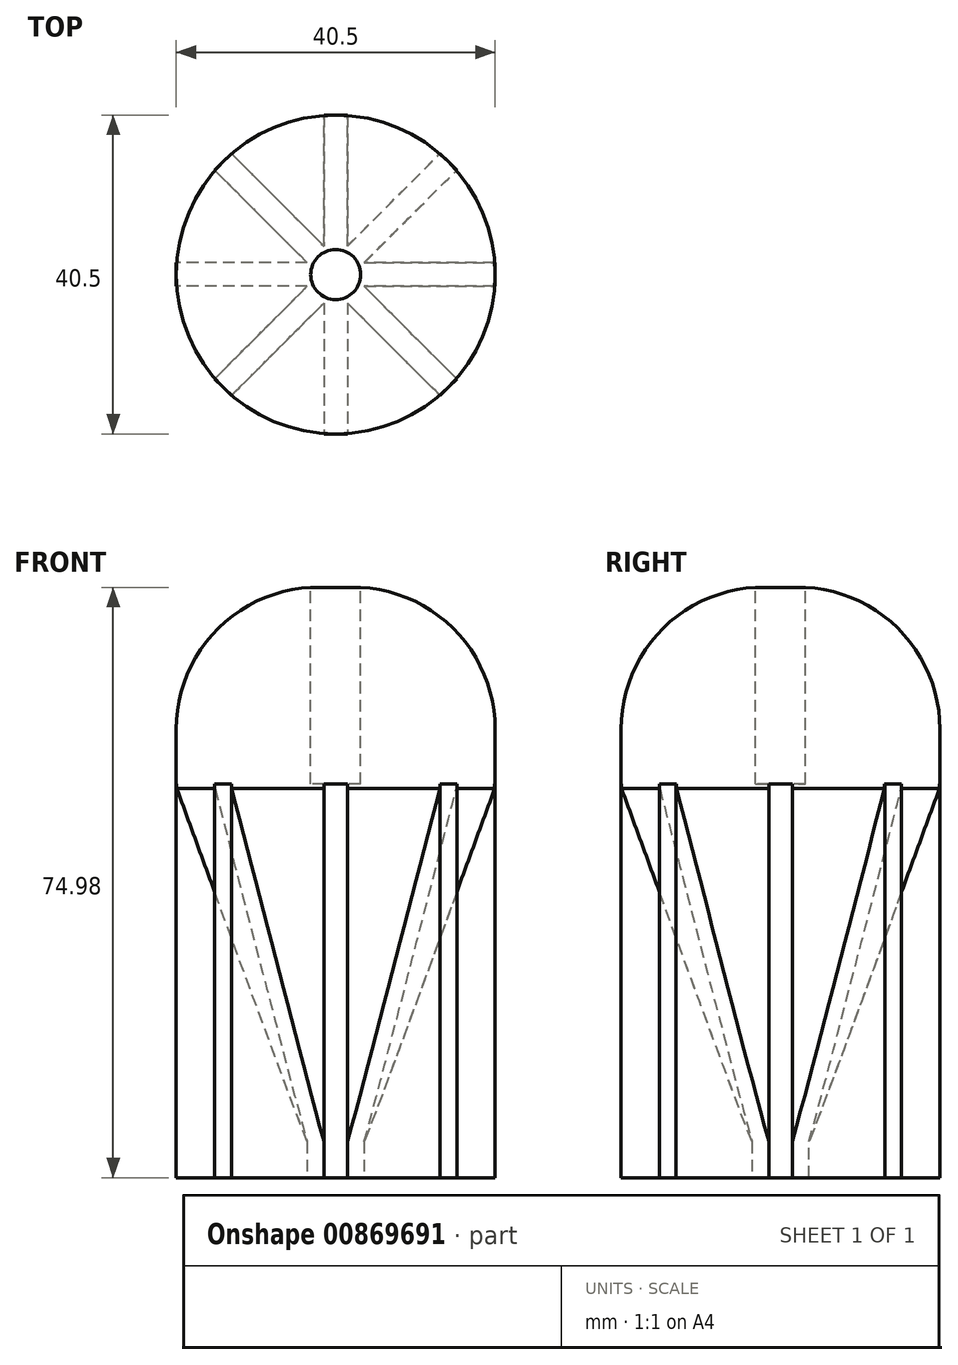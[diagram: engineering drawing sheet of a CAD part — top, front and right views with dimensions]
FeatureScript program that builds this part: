
annotation { "Feature Type Name" : "Feature", "Feature Type Description" : "" }
export const myFeature = defineFeature(function(context is Context, id is Id, definition is map)
    precondition{}
    {
        {
            var Q0;
            Q0=qCreatedBy(makeId("Top.planeOp"),FACE);
            var sketch = newSketch(context, id + "F0", { "sketchPlane" : qUnion([Q0])});
            skCircle(sketch, "E0", {"center": v(0, 0) * mm, "radius": 20.25 * mm});
            skSolve(sketch);
        }
        {
            var Q0;
            Q0 = qSketchRegion(id + "F0", true);
            extrude(context, id + "F1", {"entities" : qUnion([Q0]), "depth" : 75 * mm, "offsetDistance" : 25 * mm});
        }
        {
            var Q0;
            Q0=makeQuery(id+"F1.opExtrude","CAP_EDGE",EDGE,{"disambiguationData":[OSD([sQuery(id+"F0.wireOp",EDGE,"E0")])],"isStart":true});
            chamfer(context, id + "F2", {"entities" : qUnion([Q0]), "chamferType" : ChamferType.OFFSET_ANGLE, "width" : 18 * mm, "oppositeDirection" : true, "angle" : 70 * degree, "tangentPropagation" : true});
        }
        {
            var Q0;
            Q0=makeQuery(id+"F1.opExtrude","CAP_FACE",FACE,{"disambiguationData":[OSD([sQuery(id+"F0.wireOp",EDGE,"E0")])],"isStart":false});
            fillet(context, id + "F3", {"entities" : qUnion([Q0]), "radius" : 18 * mm, "tangentPropagation" : true, "allowEdgeOverflow" : false});
        }
        {
            var Q0;
            Q0=makeQuery(id+"F1.opExtrude","CAP_FACE",FACE,{"disambiguationData":[OSD([sQuery(id+"F0.wireOp",EDGE,"E0")])],"isStart":true});
            var sketch = newSketch(context, id + "F4", { "sketchPlane" : qUnion([Q0])});
            skCircle(sketch, "E1", {"center": v(0, 0) * mm, "radius": 20.25 * mm});
            skLineSegment(sketch, "E2", {"start": v(0, 0) * mm, "end": v(20.25, 0) * mm});
            skLineSegment(sketch, "E3", {"start": v(20.25, 0) * mm, "end": v(-20.25, 0) * mm});
            skLineSegment(sketch, "E4", {"start": v(0, 0) * mm, "end": v(0, 20.25) * mm});
            skLineSegment(sketch, "E5", {"start": v(0, 20.25) * mm, "end": v(0, -20.25) * mm});
            skLineSegment(sketch, "E6", {"start": v(0, 0) * mm, "end": v(14.32, 14.32) * mm});
            skLineSegment(sketch, "E7", {"start": v(0, 0) * mm, "end": v(-14.32, -14.32) * mm});
            skLineSegment(sketch, "E8", {"start": v(0, 0) * mm, "end": v(14.32, -14.32) * mm});
            skLineSegment(sketch, "E9", {"start": v(0, 0) * mm, "end": v(-14.32, 14.32) * mm});
            skSolve(sketch);
        }
        {
            var Q0;
            Q0=sQuery(id+"F4.wireOp",EDGE,"E6");
            extrude(context, id + "F5", {"bodyType" : ToolBodyType.SURFACE, "surfaceEntities" : qUnion([Q0]), "oppositeDirection" : true, "depth" : 50 * mm, "offsetDistance" : 25 * mm});
        }
        {
            var Q0;
            Q0=makeQuery(id+"F1.opExtrude","CAP_FACE",FACE,{"disambiguationData":[OSD([sQuery(id+"F0.wireOp",EDGE,"E0")])],"isStart":true});
            var sketch = newSketch(context, id + "F6", { "sketchPlane" : qUnion([Q0])});
            skCircle(sketch, "E10", {"center": v(0, 0) * mm, "radius": 20.25 * mm});
            skLineSegment(sketch, "E11", {"start": v(0, 0) * mm, "end": v(0, -20.25) * mm});
            skSolve(sketch);
        }
        {
            var Q0;
            Q0=sQuery(id+"F6.wireOp",EDGE,"E11");
            extrude(context, id + "F7", {"bodyType" : ToolBodyType.SURFACE, "surfaceEntities" : qUnion([Q0]), "oppositeDirection" : true, "depth" : 50 * mm, "offsetDistance" : 25 * mm});
        }
        {
            var Q0;
            Q0=makeQuery(id+"F1.opExtrude","CAP_FACE",FACE,{"disambiguationData":[OSD([sQuery(id+"F0.wireOp",EDGE,"E0")])],"isStart":true});
            var sketch = newSketch(context, id + "F8", { "sketchPlane" : qUnion([Q0])});
            skCircle(sketch, "E12", {"center": v(0, 0) * mm, "radius": 20.25 * mm});
            skLineSegment(sketch, "E13", {"start": v(0, 0) * mm, "end": v(-20.25, 0) * mm});
            skLineSegment(sketch, "E14", {"start": v(0, 0) * mm, "end": v(20.25, 0) * mm});
            skLineSegment(sketch, "E15", {"start": v(0, 0) * mm, "end": v(0, 20.25) * mm});
            skLineSegment(sketch, "E16", {"start": v(0, 0) * mm, "end": v(-14.32, 14.32) * mm});
            skLineSegment(sketch, "E17", {"start": v(0, 0) * mm, "end": v(-14.32, -14.32) * mm});
            skLineSegment(sketch, "E18", {"start": v(0, 0) * mm, "end": v(14.32, -14.32) * mm});
            skSolve(sketch);
        }
        {
            var Q0;
            Q0 = qSketchRegion(id + "F8", true);
            var Q1;
            Q1=sQuery(id+"F8.wireOp",EDGE,"E17");
            var Q2;
            Q2=sQuery(id+"F8.wireOp",EDGE,"E13");
            extrude(context, id + "F9", {"entities" : qUnion([Q0]), "bodyType" : ToolBodyType.SURFACE, "surfaceEntities" : qUnion([Q1, Q2]), "oppositeDirection" : true, "depth" : 50 * mm, "offsetDistance" : 25 * mm});
        }
        {
            var Q0;
            Q0=makeQuery(id+"F1.opExtrude","CAP_FACE",FACE,{"disambiguationData":[OSD([sQuery(id+"F0.wireOp",EDGE,"E0")])],"isStart":true});
            var sketch = newSketch(context, id + "F10", { "sketchPlane" : qUnion([Q0])});
            skCircle(sketch, "E19", {"center": v(0, 0) * mm, "radius": 20.25 * mm});
            skLineSegment(sketch, "E20", {"start": v(0, 0) * mm, "end": v(0, 20.25) * mm});
            skLineSegment(sketch, "E21", {"start": v(0, 0) * mm, "end": v(-14.32, 14.32) * mm});
            skSolve(sketch);
        }
        {
            var Q0;
            Q0=sQuery(id+"F10.wireOp",EDGE,"E21");
            var Q1;
            Q1=sQuery(id+"F10.wireOp",EDGE,"E20");
            extrude(context, id + "F11", {"bodyType" : ToolBodyType.SURFACE, "surfaceEntities" : qUnion([Q0, Q1]), "oppositeDirection" : true, "depth" : 50 * mm, "offsetDistance" : 25 * mm});
        }
        {
            var Q0;
            Q0=makeQuery(id+"F1.opExtrude","CAP_FACE",FACE,{"disambiguationData":[OSD([sQuery(id+"F0.wireOp",EDGE,"E0")])],"isStart":true});
            var sketch = newSketch(context, id + "F12", { "sketchPlane" : qUnion([Q0])});
            skCircle(sketch, "E22", {"center": v(0, 0) * mm, "radius": 20.25 * mm});
            skLineSegment(sketch, "E23", {"start": v(0, 0) * mm, "end": v(20.25, 0) * mm});
            skLineSegment(sketch, "E24", {"start": v(0, 0) * mm, "end": v(14.32, -14.32) * mm});
            skSolve(sketch);
        }
        {
            var Q0;
            Q0=sQuery(id+"F12.wireOp",EDGE,"E23");
            var Q1;
            Q1=sQuery(id+"F12.wireOp",EDGE,"E24");
            extrude(context, id + "F13", {"bodyType" : ToolBodyType.SURFACE, "surfaceEntities" : qUnion([Q0, Q1]), "oppositeDirection" : true, "depth" : 50 * mm, "offsetDistance" : 25 * mm});
        }
        {
            var Q0;
            Q0=makeQuery(id+"F7.opExtrude","SWEPT_FACE",FACE,{"disambiguationData":[OSD([sQuery(id+"F6.wireOp",EDGE,"E11")])]});
            extrude(context, id + "F14", {"entities" : qUnion([Q0]), "operationType" : NewBodyOperationType.ADD, "endBound" : BoundingType.SYMMETRIC, "depth" : 3 * mm, "offsetDistance" : 25 * mm});
        }
        {
            var Q0;
            Q0=makeQuery(id+"F9.opExtrude","SWEPT_FACE",FACE,{"disambiguationData":[OSD([sQuery(id+"F8.wireOp",EDGE,"E17")])]});
            extrude(context, id + "F15", {"entities" : qUnion([Q0]), "operationType" : NewBodyOperationType.ADD, "endBound" : BoundingType.SYMMETRIC, "depth" : 3 * mm, "offsetDistance" : 25 * mm});
        }
        {
            var Q0;
            Q0=makeQuery(id+"F9.opExtrude","SWEPT_FACE",FACE,{"disambiguationData":[OSD([sQuery(id+"F8.wireOp",EDGE,"E13")])]});
            extrude(context, id + "F16", {"entities" : qUnion([Q0]), "operationType" : NewBodyOperationType.ADD, "endBound" : BoundingType.SYMMETRIC, "depth" : 3 * mm, "offsetDistance" : 25 * mm});
        }
        {
            var Q0;
            Q0=makeQuery(id+"F11.opExtrude","SWEPT_FACE",FACE,{"disambiguationData":[OSD([sQuery(id+"F10.wireOp",EDGE,"E21")])]});
            extrude(context, id + "F17", {"entities" : qUnion([Q0]), "operationType" : NewBodyOperationType.ADD, "endBound" : BoundingType.SYMMETRIC, "depth" : 3 * mm, "offsetDistance" : 25 * mm});
        }
        {
            var Q0;
            Q0=makeQuery(id+"F11.opExtrude","SWEPT_FACE",FACE,{"disambiguationData":[OSD([sQuery(id+"F10.wireOp",EDGE,"E20")])]});
            extrude(context, id + "F18", {"entities" : qUnion([Q0]), "operationType" : NewBodyOperationType.ADD, "endBound" : BoundingType.SYMMETRIC, "depth" : 3 * mm, "offsetDistance" : 25 * mm});
        }
        {
            var Q0;
            Q0=makeQuery(id+"F13.opExtrude","SWEPT_FACE",FACE,{"disambiguationData":[OSD([sQuery(id+"F12.wireOp",EDGE,"E23")])]});
            extrude(context, id + "F19", {"entities" : qUnion([Q0]), "operationType" : NewBodyOperationType.ADD, "endBound" : BoundingType.SYMMETRIC, "depth" : 3 * mm, "offsetDistance" : 25 * mm});
        }
        {
            var Q0;
            Q0=makeQuery(id+"F5.opExtrude","SWEPT_FACE",FACE,{"disambiguationData":[OSD([sQuery(id+"F4.wireOp",EDGE,"E6")])]});
            extrude(context, id + "F20", {"entities" : qUnion([Q0]), "operationType" : NewBodyOperationType.ADD, "endBound" : BoundingType.SYMMETRIC, "depth" : 3 * mm, "offsetDistance" : 25 * mm});
        }
        {
            var Q0;
            Q0=makeQuery(id+"F13.opExtrude","SWEPT_FACE",FACE,{"disambiguationData":[OSD([sQuery(id+"F12.wireOp",EDGE,"E24")])]});
            extrude(context, id + "F21", {"entities" : qUnion([Q0]), "operationType" : NewBodyOperationType.ADD, "endBound" : BoundingType.SYMMETRIC, "depth" : 3 * mm, "offsetDistance" : 25 * mm});
        }
        {
            var Q0;
            Q0=makeQuery(id+"F1.opExtrude","CAP_FACE",FACE,{"disambiguationData":[OSD([sQuery(id+"F0.wireOp",EDGE,"E0")])],"isStart":false});
            var sketch = newSketch(context, id + "F22", { "sketchPlane" : qUnion([Q0])});
            skCircle(sketch, "E25", {"center": v(0, 0) * mm, "radius": 3.18 * mm});
            skSolve(sketch);
        }
        {
            var Q0;
            {var subQ0=sQuery(id+"F0.wireOp",EDGE,"E0");Q0=makeQuery(id+"F22.imprint","IMPRINT",FACE,{"disambiguationData":[TD([[makeQuery(id+"F22.imprint","IMPRINT",EDGE,{"derivedFrom":makeQuery(id+"F3.opFillet","BLEND_EDGE",EDGE,{"blendedFrom":[makeQuery(id+"F1.opExtrude","CAP_EDGE",EDGE,{"disambiguationData":[OSD([subQ0])],"isStart":false}),makeQuery(id+"F1.opExtrude","CAP_FACE",FACE,{"disambiguationData":[OSD([subQ0])],"isStart":false})],"blendedInto":[makeQuery(id+"F1.opExtrude","CAP_FACE",FACE,{"disambiguationData":[OSD([subQ0])],"isStart":false})]})}),1.0]])]});}
            var Q1;
            Q1=makeQuery(id+"F22.imprint","IMPRINT",FACE,{"disambiguationData":[TD([[makeQuery(id+"F22.imprint","IMPRINT",EDGE,{"derivedFrom":sQuery(id+"F22.wireOp",EDGE,"E25")}),1.0]])]});
            extrude(context, id + "F23", {"entities" : qUnion([Q0, Q1]), "operationType" : NewBodyOperationType.REMOVE, "oppositeDirection" : true, "depth" : 25 * mm, "offsetDistance" : 25 * mm});
        }
    });
